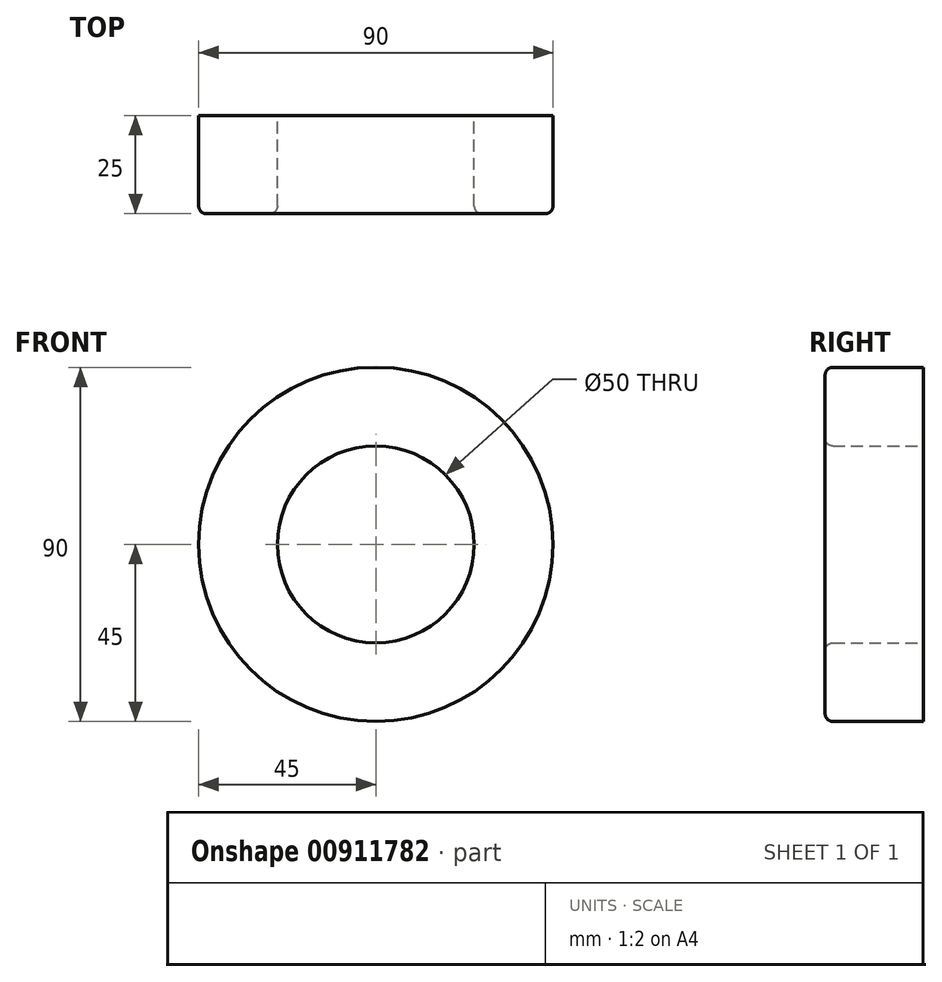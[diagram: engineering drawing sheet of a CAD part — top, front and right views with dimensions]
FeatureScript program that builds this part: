
annotation { "Feature Type Name" : "Feature", "Feature Type Description" : "" }
export const myFeature = defineFeature(function(context is Context, id is Id, definition is map)
    precondition{}
    {
        {
            var Q0;
            Q0=qCreatedBy(makeId("Front.planeOp"),FACE);
            var sketch = newSketch(context, id + "F0", { "sketchPlane" : qUnion([Q0])});
            skCircle(sketch, "E0", {"center": v(0, 0) * mm, "radius": 25 * mm});
            skCircle(sketch, "E1", {"center": v(0, 0) * mm, "radius": 45 * mm});
            skSolve(sketch);
        }
        {
            var Q0;
            Q0=makeQuery(id+"F0.imprint","IMPRINT",FACE,{"disambiguationData":[TD([[makeQuery(id+"F0.imprint","IMPRINT",EDGE,{"derivedFrom":sQuery(id+"F0.wireOp",EDGE,"E0")}),-1.0]])]});
            extrude(context, id + "F1", {"entities" : qUnion([Q0]), "depth" : 25 * mm, "offsetDistance" : 25 * mm});
        }
        {
            var Q0;
            Q0=makeQuery(id+"F1.opExtrude","CAP_EDGE",EDGE,{"disambiguationData":[OSD([sQuery(id+"F0.wireOp",EDGE,"E1")])],"isStart":false});
            fillet(context, id + "F2", {"entities" : qUnion([Q0]), "radius" : 2 * mm, "tangentPropagation" : true, "allowEdgeOverflow" : false});
        }
        {
            var Q0;
            Q0=makeQuery(id+"F1.opExtrude","CAP_EDGE",EDGE,{"disambiguationData":[OSD([sQuery(id+"F0.wireOp",EDGE,"E0")])],"isStart":false});
            fillet(context, id + "F3", {"entities" : qUnion([Q0]), "radius" : 2 * mm, "tangentPropagation" : true, "allowEdgeOverflow" : false});
        }
    });
